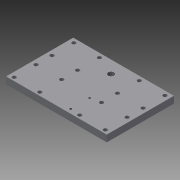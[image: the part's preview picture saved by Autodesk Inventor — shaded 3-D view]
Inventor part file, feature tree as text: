
AUTODESK INVENTOR PART (.ipt)
format: ipt  version: 2015 SP1 (Build 190203100, 203)  size: 304,128 bytes
history: native  units: mm
features: hole x5, pattern_linear x3, extrude x1, sketch x1
ambient origin geometry x8: Origin, YZ Plane, XZ Plane, XY Plane, X Axis, Y Axis, Z Axis, Center Point
bodies: Solid1 (feature_tree)
feature tree (10):
  extrude  "Extrusion1"  Depth=8.0mm
  hole  "Hole1"  [1 undecoded]
  pattern_linear  "Rectangular Pattern1"  Spacing1=5.0mm  [1 undecoded]
  hole  "Hole2"  [1 undecoded]
  pattern_linear  "Rectangular Pattern2"  Count1=2 Spacing1=45.0mm
  pattern_linear  "Rectangular Pattern3"  Count1=6 Spacing1=15.0mm
  hole  "Hole3"  [1 undecoded]
  hole  "Hole4"  [1 undecoded]
  hole  "Hole5"  [1 undecoded]
  sketch  "Sketch1"  dims[d2=8.0mm d3=0.0mm d4=5.0mm d5=36.25mm d6=4.5mm d7=6.0mm d8=4.0mm d9=2.0mm d10=90.0deg d11=8.0mm d12=20.594885mm d13=20.0mm d15=30.5mm d16=20.0mm d18=26.0mm d19=5.0mm d20=36.25mm d21=4.5mm d22=6.0mm d23=4.0mm d24=2.0mm d25=90.0deg d26=8.0mm d27=20.594885mm d28=20.0mm d30=30.5mm d31=20.0mm d33=26.0mm d34=20.0mm d36=45.0mm d37=60.0mm d38=15.0mm d39=6.647mm d40=16.0mm d41=4.0mm d42=2.0mm d43=90.0deg d44=22.2mm d45=20.594885mm d46=5.0mm d47=48.0mm d48=2.459mm d49=6.0mm d50=4.0mm d51=2.0mm d52=90.0deg d53=8.8mm d54=20.594885mm d55=27.5mm d56=48.0mm d57=2.459mm d58=6.0mm d59=4.0mm d60=2.0mm d61=90.0deg d62=8.8mm d63=20.594885mm]
note: 6 required parameter values undecoded (feature->parameter linkage not recoverable at this tier; creation-order binding heuristic only, values carry confidence <= 0.55)
